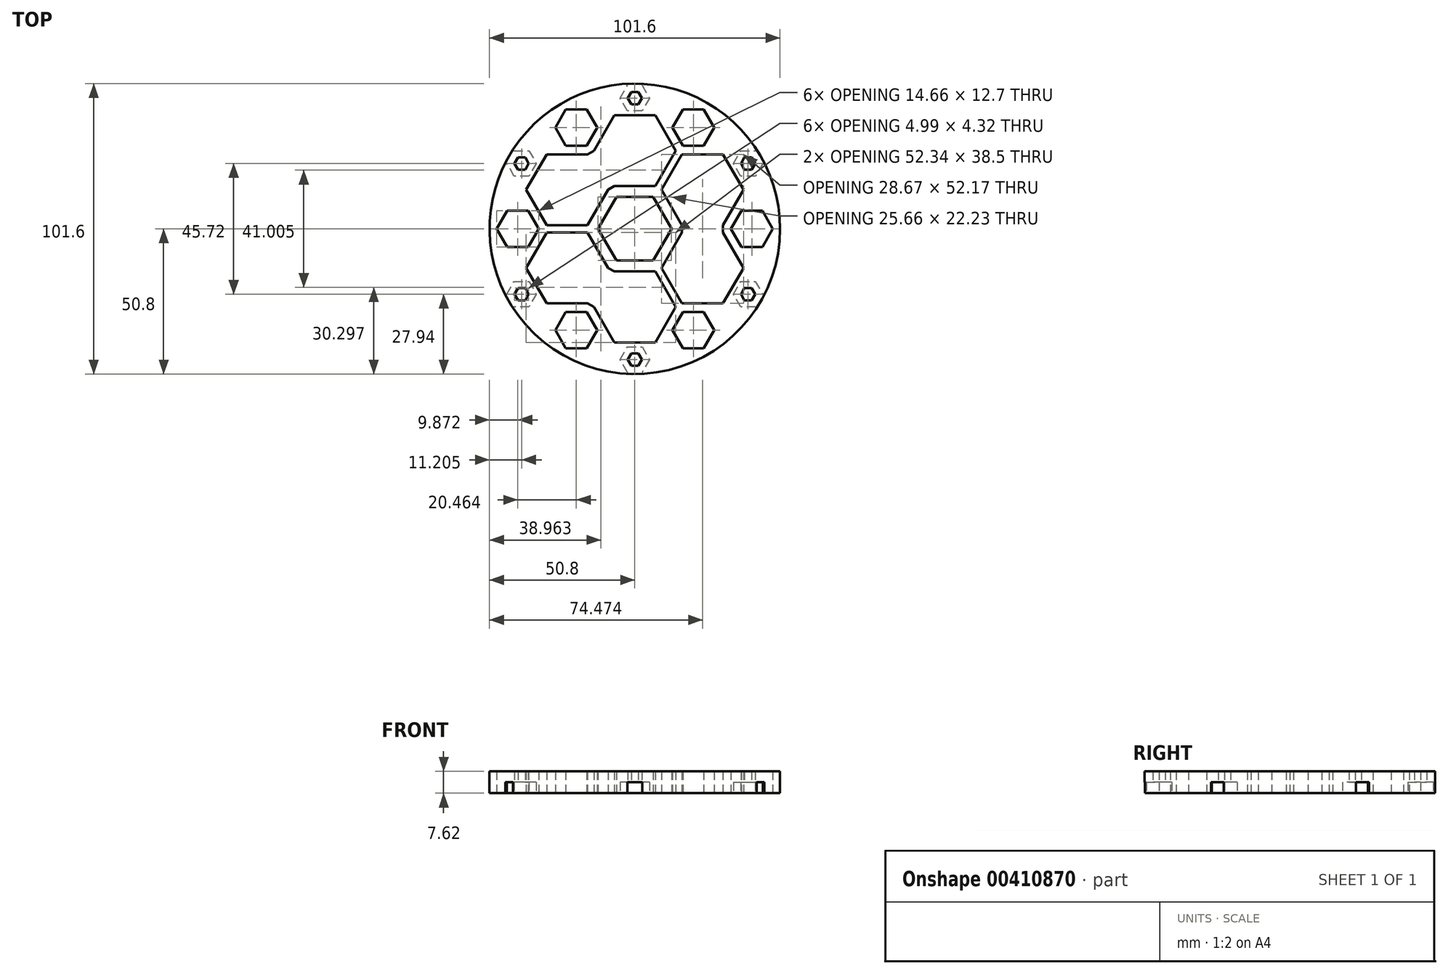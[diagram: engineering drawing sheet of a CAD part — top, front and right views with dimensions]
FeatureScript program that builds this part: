
annotation { "Feature Type Name" : "Feature", "Feature Type Description" : "" }
export const myFeature = defineFeature(function(context is Context, id is Id, definition is map)
    precondition{}
    {
        {
            var Q0;
            Q0=qCreatedBy(makeId("Top.planeOp"),FACE);
            var sketch = newSketch(context, id + "F0", { "sketchPlane" : qUnion([Q0])});
            skCircle(sketch, "E0", {"center": v(0, 0) * mm, "radius": 50.8 * mm});
            skCircle(sketch, "E1.cCircle", {"center": v(0, 0) * mm, "radius": 11.11 * mm, "construction": true});
            skLineSegment(sketch, "E1.0", {"start": v(-6.42, 11.11) * mm, "end": v(6.42, 11.11) * mm});
            skLineSegment(sketch, "E1.1", {"start": v(6.42, 11.11) * mm, "end": v(12.83, 0) * mm});
            skLineSegment(sketch, "E1.2", {"start": v(12.83, 0) * mm, "end": v(6.42, -11.11) * mm});
            skLineSegment(sketch, "E1.3", {"start": v(6.42, -11.11) * mm, "end": v(-6.42, -11.11) * mm});
            skLineSegment(sketch, "E1.4", {"start": v(-6.42, -11.11) * mm, "end": v(-12.83, 0) * mm});
            skLineSegment(sketch, "E1.5", {"start": v(-12.83, 0) * mm, "end": v(-6.42, 11.11) * mm});
            skPoint(sketch, "E1.0.midPoint", {"position": v(0, 11.11) * mm});
            skLineSegment(sketch, "E2", {"start": v(0, 0) * mm, "end": v(0, 45.72) * mm, "construction": true});
            skCircle(sketch, "E3.cCircle", {"center": v(0, 45.72) * mm, "radius": 2.16 * mm, "construction": true});
            skLineSegment(sketch, "E3.0", {"start": v(-1.25, 47.88) * mm, "end": v(1.25, 47.88) * mm});
            skLineSegment(sketch, "E3.1", {"start": v(1.25, 47.88) * mm, "end": v(2.5, 45.72) * mm});
            skLineSegment(sketch, "E3.2", {"start": v(2.5, 45.72) * mm, "end": v(1.25, 43.56) * mm});
            skLineSegment(sketch, "E3.3", {"start": v(1.25, 43.56) * mm, "end": v(-1.25, 43.56) * mm});
            skLineSegment(sketch, "E3.4", {"start": v(-1.25, 43.56) * mm, "end": v(-2.5, 45.72) * mm});
            skLineSegment(sketch, "E3.5", {"start": v(-2.5, 45.72) * mm, "end": v(-1.25, 47.88) * mm});
            skPoint(sketch, "E3.0.midPoint", {"position": v(0, 47.88) * mm});
            skLineSegment(sketch, "E4", {"start": v(0, 0) * mm, "end": v(39.6, -22.86) * mm, "construction": true});
            skCircle(sketch, "E5.cCircle", {"center": v(0, 27.34) * mm, "radius": 12.41 * mm, "construction": true});
            skLineSegment(sketch, "E5.0", {"start": v(-7.17, 39.75) * mm, "end": v(7.17, 39.75) * mm});
            skLineSegment(sketch, "E5.1", {"start": v(7.17, 39.75) * mm, "end": v(14.33, 27.34) * mm});
            skLineSegment(sketch, "E5.2", {"start": v(14.33, 27.34) * mm, "end": v(7.17, 14.92) * mm});
            skLineSegment(sketch, "E5.3", {"start": v(7.17, 14.92) * mm, "end": v(-7.17, 14.92) * mm});
            skLineSegment(sketch, "E5.4", {"start": v(-7.17, 14.92) * mm, "end": v(-14.33, 27.34) * mm});
            skLineSegment(sketch, "E5.5", {"start": v(-14.33, 27.34) * mm, "end": v(-7.17, 39.75) * mm});
            skPoint(sketch, "E5.0.midPoint", {"position": v(0, 39.75) * mm});
            skLineSegment(sketch, "E6.1.0", {"start": v(-38.35, 20.7) * mm, "end": v(-40.84, 20.7) * mm});
            skLineSegment(sketch, "E6.1.1", {"start": v(-37.1, 22.86) * mm, "end": v(-38.35, 20.7) * mm});
            skLineSegment(sketch, "E6.1.2", {"start": v(-38.35, 25.02) * mm, "end": v(-37.1, 22.86) * mm});
            skLineSegment(sketch, "E6.1.3", {"start": v(-40.84, 25.02) * mm, "end": v(-38.35, 25.02) * mm});
            skLineSegment(sketch, "E6.1.4", {"start": v(-42.09, 22.86) * mm, "end": v(-40.84, 25.02) * mm});
            skLineSegment(sketch, "E6.1.5", {"start": v(-40.84, 20.7) * mm, "end": v(-42.09, 22.86) * mm});
            skLineSegment(sketch, "E6.1.6", {"start": v(-16.5, 26.08) * mm, "end": v(-9.34, 13.67) * mm});
            skLineSegment(sketch, "E6.1.7", {"start": v(-30.84, 26.08) * mm, "end": v(-16.5, 26.08) * mm});
            skLineSegment(sketch, "E6.1.8", {"start": v(-38, 13.67) * mm, "end": v(-30.84, 26.08) * mm});
            skLineSegment(sketch, "E6.1.9", {"start": v(-30.84, 1.25) * mm, "end": v(-38, 13.67) * mm});
            skLineSegment(sketch, "E6.1.10", {"start": v(-16.5, 1.25) * mm, "end": v(-30.84, 1.25) * mm});
            skLineSegment(sketch, "E6.1.11", {"start": v(-9.34, 13.67) * mm, "end": v(-16.5, 1.25) * mm});
            skLineSegment(sketch, "E6.2.0", {"start": v(-37.1, -22.86) * mm, "end": v(-38.35, -25.02) * mm});
            skLineSegment(sketch, "E6.2.1", {"start": v(-38.35, -20.7) * mm, "end": v(-37.1, -22.86) * mm});
            skLineSegment(sketch, "E6.2.2", {"start": v(-40.84, -20.7) * mm, "end": v(-38.35, -20.7) * mm});
            skLineSegment(sketch, "E6.2.3", {"start": v(-42.09, -22.86) * mm, "end": v(-40.84, -20.7) * mm});
            skLineSegment(sketch, "E6.2.4", {"start": v(-40.84, -25.02) * mm, "end": v(-42.09, -22.86) * mm});
            skLineSegment(sketch, "E6.2.5", {"start": v(-38.35, -25.02) * mm, "end": v(-40.84, -25.02) * mm});
            skLineSegment(sketch, "E6.2.6", {"start": v(-30.84, -1.25) * mm, "end": v(-16.5, -1.25) * mm});
            skLineSegment(sketch, "E6.2.7", {"start": v(-38, -13.67) * mm, "end": v(-30.84, -1.25) * mm});
            skLineSegment(sketch, "E6.2.8", {"start": v(-30.84, -26.08) * mm, "end": v(-38, -13.67) * mm});
            skLineSegment(sketch, "E6.2.9", {"start": v(-16.5, -26.08) * mm, "end": v(-30.84, -26.08) * mm});
            skLineSegment(sketch, "E6.2.10", {"start": v(-9.34, -13.67) * mm, "end": v(-16.5, -26.08) * mm});
            skLineSegment(sketch, "E6.2.11", {"start": v(-16.5, -1.25) * mm, "end": v(-9.34, -13.67) * mm});
            skLineSegment(sketch, "E7.1.3.0", {"start": v(1.25, -43.56) * mm, "end": v(2.5, -45.72) * mm});
            skLineSegment(sketch, "E7.3.3.0", {"start": v(-1.25, -43.56) * mm, "end": v(1.25, -43.56) * mm});
            skLineSegment(sketch, "E7.6.3.0", {"start": v(-2.5, -45.72) * mm, "end": v(-1.25, -43.56) * mm});
            skLineSegment(sketch, "E7.9.3.0", {"start": v(-1.25, -47.88) * mm, "end": v(-2.5, -45.72) * mm});
            skLineSegment(sketch, "E7.12.3.0", {"start": v(1.25, -47.88) * mm, "end": v(-1.25, -47.88) * mm});
            skLineSegment(sketch, "E7.15.3.0", {"start": v(2.5, -45.72) * mm, "end": v(1.25, -47.88) * mm});
            skLineSegment(sketch, "E7.18.3.0", {"start": v(-14.33, -27.34) * mm, "end": v(-7.17, -14.92) * mm});
            skLineSegment(sketch, "E7.21.3.0", {"start": v(-7.17, -39.75) * mm, "end": v(-14.33, -27.34) * mm});
            skLineSegment(sketch, "E7.24.3.0", {"start": v(7.17, -39.75) * mm, "end": v(-7.17, -39.75) * mm});
            skLineSegment(sketch, "E7.27.3.0", {"start": v(14.33, -27.34) * mm, "end": v(7.17, -39.75) * mm});
            skLineSegment(sketch, "E7.30.3.0", {"start": v(7.17, -14.92) * mm, "end": v(14.33, -27.34) * mm});
            skLineSegment(sketch, "E7.33.3.0", {"start": v(-7.17, -14.92) * mm, "end": v(7.17, -14.92) * mm});
            skLineSegment(sketch, "E7.1.4.0", {"start": v(38.35, -20.7) * mm, "end": v(40.84, -20.7) * mm});
            skLineSegment(sketch, "E7.3.4.0", {"start": v(37.1, -22.86) * mm, "end": v(38.35, -20.7) * mm});
            skLineSegment(sketch, "E7.6.4.0", {"start": v(38.35, -25.02) * mm, "end": v(37.1, -22.86) * mm});
            skLineSegment(sketch, "E7.9.4.0", {"start": v(40.84, -25.02) * mm, "end": v(38.35, -25.02) * mm});
            skLineSegment(sketch, "E7.12.4.0", {"start": v(42.09, -22.86) * mm, "end": v(40.84, -25.02) * mm});
            skLineSegment(sketch, "E7.15.4.0", {"start": v(40.84, -20.7) * mm, "end": v(42.09, -22.86) * mm});
            skLineSegment(sketch, "E7.18.4.0", {"start": v(16.5, -26.08) * mm, "end": v(9.34, -13.67) * mm});
            skLineSegment(sketch, "E7.21.4.0", {"start": v(30.84, -26.08) * mm, "end": v(16.5, -26.08) * mm});
            skLineSegment(sketch, "E7.24.4.0", {"start": v(38, -13.67) * mm, "end": v(30.84, -26.08) * mm});
            skLineSegment(sketch, "E7.27.4.0", {"start": v(30.84, -1.25) * mm, "end": v(38, -13.67) * mm});
            skLineSegment(sketch, "E7.30.4.0", {"start": v(16.5, -1.25) * mm, "end": v(30.84, -1.25) * mm});
            skLineSegment(sketch, "E7.33.4.0", {"start": v(9.34, -13.67) * mm, "end": v(16.5, -1.25) * mm});
            skLineSegment(sketch, "E7.1.5.0", {"start": v(37.1, 22.86) * mm, "end": v(38.35, 25.02) * mm});
            skLineSegment(sketch, "E7.3.5.0", {"start": v(38.35, 20.7) * mm, "end": v(37.1, 22.86) * mm});
            skLineSegment(sketch, "E7.6.5.0", {"start": v(40.84, 20.7) * mm, "end": v(38.35, 20.7) * mm});
            skLineSegment(sketch, "E7.9.5.0", {"start": v(42.09, 22.86) * mm, "end": v(40.84, 20.7) * mm});
            skLineSegment(sketch, "E7.12.5.0", {"start": v(40.84, 25.02) * mm, "end": v(42.09, 22.86) * mm});
            skLineSegment(sketch, "E7.15.5.0", {"start": v(38.35, 25.02) * mm, "end": v(40.84, 25.02) * mm});
            skLineSegment(sketch, "E7.18.5.0", {"start": v(30.84, 1.25) * mm, "end": v(16.5, 1.25) * mm});
            skLineSegment(sketch, "E7.21.5.0", {"start": v(38, 13.67) * mm, "end": v(30.84, 1.25) * mm});
            skLineSegment(sketch, "E7.24.5.0", {"start": v(30.84, 26.08) * mm, "end": v(38, 13.67) * mm});
            skLineSegment(sketch, "E7.27.5.0", {"start": v(16.5, 26.08) * mm, "end": v(30.84, 26.08) * mm});
            skLineSegment(sketch, "E7.30.5.0", {"start": v(9.34, 13.67) * mm, "end": v(16.5, 26.08) * mm});
            skLineSegment(sketch, "E7.33.5.0", {"start": v(16.5, 1.25) * mm, "end": v(9.34, 13.67) * mm});
            skLineSegment(sketch, "E8", {"start": v(-6.42, 11.11) * mm, "end": v(-25.4, 44) * mm, "construction": true});
            skCircle(sketch, "E9.cCircle", {"center": v(-20.46, 35.44) * mm, "radius": 6.35 * mm, "construction": true});
            skLineSegment(sketch, "E9.0", {"start": v(-16.8, 41.8) * mm, "end": v(-13.13, 35.44) * mm});
            skLineSegment(sketch, "E9.1", {"start": v(-13.13, 35.44) * mm, "end": v(-16.8, 29.1) * mm});
            skLineSegment(sketch, "E9.2", {"start": v(-16.8, 29.1) * mm, "end": v(-24.13, 29.1) * mm});
            skLineSegment(sketch, "E9.3", {"start": v(-24.13, 29.1) * mm, "end": v(-27.8, 35.44) * mm});
            skLineSegment(sketch, "E9.4", {"start": v(-27.8, 35.44) * mm, "end": v(-24.13, 41.8) * mm});
            skLineSegment(sketch, "E9.5", {"start": v(-24.13, 41.8) * mm, "end": v(-16.8, 41.8) * mm});
            skPoint(sketch, "E9.0.midPoint", {"position": v(-14.96, 38.62) * mm});
            skLineSegment(sketch, "E10.1.0", {"start": v(-48.26, 0) * mm, "end": v(-44.6, 6.35) * mm});
            skLineSegment(sketch, "E10.1.1", {"start": v(-44.6, 6.35) * mm, "end": v(-37.26, 6.35) * mm});
            skLineSegment(sketch, "E10.1.2", {"start": v(-37.26, 6.35) * mm, "end": v(-33.6, 0) * mm});
            skLineSegment(sketch, "E10.1.3", {"start": v(-33.6, 0) * mm, "end": v(-37.26, -6.35) * mm});
            skLineSegment(sketch, "E10.1.4", {"start": v(-37.26, -6.35) * mm, "end": v(-44.6, -6.35) * mm});
            skLineSegment(sketch, "E10.1.5", {"start": v(-44.6, -6.35) * mm, "end": v(-48.26, 0) * mm});
            skLineSegment(sketch, "E10.2.0", {"start": v(-24.13, -41.8) * mm, "end": v(-27.8, -35.44) * mm});
            skLineSegment(sketch, "E10.2.1", {"start": v(-27.8, -35.44) * mm, "end": v(-24.13, -29.1) * mm});
            skLineSegment(sketch, "E10.2.2", {"start": v(-24.13, -29.1) * mm, "end": v(-16.8, -29.1) * mm});
            skLineSegment(sketch, "E10.2.3", {"start": v(-16.8, -29.1) * mm, "end": v(-13.13, -35.44) * mm});
            skLineSegment(sketch, "E10.2.4", {"start": v(-13.13, -35.44) * mm, "end": v(-16.8, -41.8) * mm});
            skLineSegment(sketch, "E10.2.5", {"start": v(-16.8, -41.8) * mm, "end": v(-24.13, -41.8) * mm});
            skLineSegment(sketch, "E10.3.0", {"start": v(24.13, -41.8) * mm, "end": v(16.8, -41.8) * mm});
            skLineSegment(sketch, "E10.3.1", {"start": v(16.8, -41.8) * mm, "end": v(13.13, -35.44) * mm});
            skLineSegment(sketch, "E10.3.2", {"start": v(13.13, -35.44) * mm, "end": v(16.8, -29.1) * mm});
            skLineSegment(sketch, "E10.3.3", {"start": v(16.8, -29.1) * mm, "end": v(24.13, -29.1) * mm});
            skLineSegment(sketch, "E10.3.4", {"start": v(24.13, -29.1) * mm, "end": v(27.8, -35.44) * mm});
            skLineSegment(sketch, "E10.3.5", {"start": v(27.8, -35.44) * mm, "end": v(24.13, -41.8) * mm});
            skLineSegment(sketch, "E10.4.0", {"start": v(48.26, 0) * mm, "end": v(44.6, -6.35) * mm});
            skLineSegment(sketch, "E10.4.1", {"start": v(44.6, -6.35) * mm, "end": v(37.26, -6.35) * mm});
            skLineSegment(sketch, "E10.4.2", {"start": v(37.26, -6.35) * mm, "end": v(33.6, 0) * mm});
            skLineSegment(sketch, "E10.4.3", {"start": v(33.6, 0) * mm, "end": v(37.26, 6.35) * mm});
            skLineSegment(sketch, "E10.4.4", {"start": v(37.26, 6.35) * mm, "end": v(44.6, 6.35) * mm});
            skLineSegment(sketch, "E10.4.5", {"start": v(44.6, 6.35) * mm, "end": v(48.26, 0) * mm});
            skLineSegment(sketch, "E10.5.0", {"start": v(24.13, 41.8) * mm, "end": v(27.8, 35.44) * mm});
            skLineSegment(sketch, "E10.5.1", {"start": v(27.8, 35.44) * mm, "end": v(24.13, 29.1) * mm});
            skLineSegment(sketch, "E10.5.2", {"start": v(24.13, 29.1) * mm, "end": v(16.8, 29.1) * mm});
            skLineSegment(sketch, "E10.5.3", {"start": v(16.8, 29.1) * mm, "end": v(13.13, 35.44) * mm});
            skLineSegment(sketch, "E10.5.4", {"start": v(13.13, 35.44) * mm, "end": v(16.8, 41.8) * mm});
            skLineSegment(sketch, "E10.5.5", {"start": v(16.8, 41.8) * mm, "end": v(24.13, 41.8) * mm});
            skCircle(sketch, "E11.cCircle", {"center": v(0, 45.72) * mm, "radius": 4.45 * mm, "construction": true});
            skLineSegment(sketch, "E11.0", {"start": v(-2.57, 50.16) * mm, "end": v(2.57, 50.16) * mm});
            skLineSegment(sketch, "E11.1", {"start": v(2.57, 50.16) * mm, "end": v(5.13, 45.72) * mm});
            skLineSegment(sketch, "E11.2", {"start": v(5.13, 45.72) * mm, "end": v(2.57, 41.28) * mm});
            skLineSegment(sketch, "E11.3", {"start": v(2.57, 41.28) * mm, "end": v(-2.57, 41.28) * mm});
            skLineSegment(sketch, "E11.4", {"start": v(-2.57, 41.28) * mm, "end": v(-5.13, 45.72) * mm});
            skLineSegment(sketch, "E11.5", {"start": v(-5.13, 45.72) * mm, "end": v(-2.57, 50.16) * mm});
            skPoint(sketch, "E11.0.midPoint", {"position": v(0, 50.16) * mm});
            skLineSegment(sketch, "E12.1.0", {"start": v(-44.73, 22.86) * mm, "end": v(-42.16, 27.3) * mm});
            skLineSegment(sketch, "E12.1.1", {"start": v(-42.16, 18.42) * mm, "end": v(-44.73, 22.86) * mm});
            skLineSegment(sketch, "E12.1.2", {"start": v(-37.03, 18.42) * mm, "end": v(-42.16, 18.42) * mm});
            skLineSegment(sketch, "E12.1.3", {"start": v(-34.46, 22.86) * mm, "end": v(-37.03, 18.42) * mm});
            skLineSegment(sketch, "E12.1.4", {"start": v(-37.03, 27.3) * mm, "end": v(-34.46, 22.86) * mm});
            skLineSegment(sketch, "E12.1.5", {"start": v(-42.16, 27.3) * mm, "end": v(-37.03, 27.3) * mm});
            skLineSegment(sketch, "E12.2.0", {"start": v(-42.16, -27.3) * mm, "end": v(-44.73, -22.86) * mm});
            skLineSegment(sketch, "E12.2.1", {"start": v(-37.03, -27.3) * mm, "end": v(-42.16, -27.3) * mm});
            skLineSegment(sketch, "E12.2.2", {"start": v(-34.46, -22.86) * mm, "end": v(-37.03, -27.3) * mm});
            skLineSegment(sketch, "E12.2.3", {"start": v(-37.03, -18.41) * mm, "end": v(-34.46, -22.86) * mm});
            skLineSegment(sketch, "E12.2.4", {"start": v(-42.16, -18.41) * mm, "end": v(-37.03, -18.41) * mm});
            skLineSegment(sketch, "E12.2.5", {"start": v(-44.73, -22.86) * mm, "end": v(-42.16, -18.41) * mm});
            skLineSegment(sketch, "E13.1.3.0", {"start": v(2.57, -50.16) * mm, "end": v(-2.57, -50.16) * mm});
            skLineSegment(sketch, "E13.3.3.0", {"start": v(5.13, -45.72) * mm, "end": v(2.57, -50.16) * mm});
            skLineSegment(sketch, "E13.6.3.0", {"start": v(2.57, -41.28) * mm, "end": v(5.13, -45.72) * mm});
            skLineSegment(sketch, "E13.9.3.0", {"start": v(-2.57, -41.28) * mm, "end": v(2.57, -41.28) * mm});
            skLineSegment(sketch, "E13.12.3.0", {"start": v(-5.13, -45.72) * mm, "end": v(-2.57, -41.28) * mm});
            skLineSegment(sketch, "E13.15.3.0", {"start": v(-2.57, -50.16) * mm, "end": v(-5.13, -45.72) * mm});
            skLineSegment(sketch, "E13.1.4.0", {"start": v(44.73, -22.86) * mm, "end": v(42.16, -27.3) * mm});
            skLineSegment(sketch, "E13.3.4.0", {"start": v(42.16, -18.42) * mm, "end": v(44.73, -22.86) * mm});
            skLineSegment(sketch, "E13.6.4.0", {"start": v(37.03, -18.42) * mm, "end": v(42.16, -18.42) * mm});
            skLineSegment(sketch, "E13.9.4.0", {"start": v(34.46, -22.86) * mm, "end": v(37.03, -18.42) * mm});
            skLineSegment(sketch, "E13.12.4.0", {"start": v(37.03, -27.3) * mm, "end": v(34.46, -22.86) * mm});
            skLineSegment(sketch, "E13.15.4.0", {"start": v(42.16, -27.3) * mm, "end": v(37.03, -27.3) * mm});
            skLineSegment(sketch, "E13.1.5.0", {"start": v(42.16, 27.3) * mm, "end": v(44.73, 22.86) * mm});
            skLineSegment(sketch, "E13.3.5.0", {"start": v(37.03, 27.3) * mm, "end": v(42.16, 27.3) * mm});
            skLineSegment(sketch, "E13.6.5.0", {"start": v(34.46, 22.86) * mm, "end": v(37.03, 27.3) * mm});
            skLineSegment(sketch, "E13.9.5.0", {"start": v(37.03, 18.42) * mm, "end": v(34.46, 22.86) * mm});
            skLineSegment(sketch, "E13.12.5.0", {"start": v(42.16, 18.42) * mm, "end": v(37.03, 18.42) * mm});
            skLineSegment(sketch, "E13.15.5.0", {"start": v(44.73, 22.86) * mm, "end": v(42.16, 18.42) * mm});
            skLineSegment(sketch, "E14", {"start": v(-44.73, 22.86) * mm, "end": v(-45.22, 23.15) * mm});
            skLineSegment(sketch, "E15", {"start": v(-42.16, 27.3) * mm, "end": v(-42.65, 27.6) * mm});
            skLineSegment(sketch, "E16.1.0", {"start": v(-42.16, -27.3) * mm, "end": v(-42.65, -27.6) * mm});
            skLineSegment(sketch, "E16.1.1", {"start": v(-44.73, -22.86) * mm, "end": v(-45.22, -23.15) * mm});
            skLineSegment(sketch, "E16.2.0", {"start": v(2.57, -50.16) * mm, "end": v(2.57, -50.74) * mm});
            skLineSegment(sketch, "E16.2.1", {"start": v(-2.57, -50.16) * mm, "end": v(-2.57, -50.74) * mm});
            skLineSegment(sketch, "E16.3.0", {"start": v(44.73, -22.86) * mm, "end": v(45.22, -23.15) * mm});
            skLineSegment(sketch, "E16.3.1", {"start": v(42.16, -27.3) * mm, "end": v(42.65, -27.6) * mm});
            skLineSegment(sketch, "E16.4.0", {"start": v(42.16, 27.3) * mm, "end": v(42.65, 27.6) * mm});
            skLineSegment(sketch, "E16.4.1", {"start": v(44.73, 22.86) * mm, "end": v(45.22, 23.15) * mm});
            skLineSegment(sketch, "E16.5.0", {"start": v(-2.57, 50.16) * mm, "end": v(-2.57, 50.74) * mm});
            skLineSegment(sketch, "E16.5.1", {"start": v(2.57, 50.16) * mm, "end": v(2.57, 50.74) * mm});
            skSolve(sketch);
        }
        {
            var Q0;
            Q0=makeQuery(id+"F0.imprint","IMPRINT",FACE,{"disambiguationData":[TD([[makeQuery(id+"F0.imprint","IMPRINT",EDGE,{"derivedFrom":sQuery(id+"F0.wireOp",EDGE,"E0")}),1.0]])]});
            var Q1;
            Q1=makeQuery(id+"F0.imprint","IMPRINT",FACE,{"disambiguationData":[TD([[makeQuery(id+"F0.imprint","IMPRINT",EDGE,{"derivedFrom":sQuery(id+"F0.wireOp",EDGE,"E3.0")}),1.0]])]});
            var Q2;
            Q2=makeQuery(id+"F0.imprint","IMPRINT",FACE,{"disambiguationData":[TD([[makeQuery(id+"F0.imprint","IMPRINT",EDGE,{"derivedFrom":sQuery(id+"F0.wireOp",EDGE,"E7.1.5.0")}),1.0]])]});
            var Q3;
            Q3=makeQuery(id+"F0.imprint","IMPRINT",FACE,{"disambiguationData":[TD([[makeQuery(id+"F0.imprint","IMPRINT",EDGE,{"derivedFrom":sQuery(id+"F0.wireOp",EDGE,"E7.1.4.0")}),1.0]])]});
            var Q4;
            Q4=makeQuery(id+"F0.imprint","IMPRINT",FACE,{"disambiguationData":[TD([[makeQuery(id+"F0.imprint","IMPRINT",EDGE,{"derivedFrom":sQuery(id+"F0.wireOp",EDGE,"E7.1.3.0")}),1.0]])]});
            var Q5;
            Q5=makeQuery(id+"F0.imprint","IMPRINT",FACE,{"disambiguationData":[TD([[makeQuery(id+"F0.imprint","IMPRINT",EDGE,{"derivedFrom":sQuery(id+"F0.wireOp",EDGE,"E6.2.0")}),1.0]])]});
            var Q6;
            Q6=makeQuery(id+"F0.imprint","IMPRINT",FACE,{"disambiguationData":[TD([[makeQuery(id+"F0.imprint","IMPRINT",EDGE,{"derivedFrom":sQuery(id+"F0.wireOp",EDGE,"E6.1.0")}),1.0]])]});
            var Q7;
            Q7=makeQuery(id+"F0.imprint","IMPRINT",FACE,{"disambiguationData":[TD([[makeQuery(id+"F0.imprint","IMPRINT",EDGE,{"derivedFrom":sQuery(id+"F0.wireOp",EDGE,"E12.1.0")}),1.0]])]});
            var Q8;
            Q8=makeQuery(id+"F0.imprint","IMPRINT",FACE,{"disambiguationData":[TD([[makeQuery(id+"F0.imprint","IMPRINT",EDGE,{"derivedFrom":sQuery(id+"F0.wireOp",EDGE,"E12.2.0")}),1.0]])]});
            var Q9;
            Q9=makeQuery(id+"F0.imprint","IMPRINT",FACE,{"disambiguationData":[TD([[makeQuery(id+"F0.imprint","IMPRINT",EDGE,{"derivedFrom":sQuery(id+"F0.wireOp",EDGE,"E13.1.3.0")}),1.0]])]});
            var Q10;
            Q10=makeQuery(id+"F0.imprint","IMPRINT",FACE,{"disambiguationData":[TD([[makeQuery(id+"F0.imprint","IMPRINT",EDGE,{"derivedFrom":sQuery(id+"F0.wireOp",EDGE,"E13.1.4.0")}),1.0]])]});
            var Q11;
            Q11=makeQuery(id+"F0.imprint","IMPRINT",FACE,{"disambiguationData":[TD([[makeQuery(id+"F0.imprint","IMPRINT",EDGE,{"derivedFrom":sQuery(id+"F0.wireOp",EDGE,"E13.1.5.0")}),1.0]])]});
            var Q12;
            Q12=makeQuery(id+"F0.imprint","IMPRINT",FACE,{"disambiguationData":[TD([[makeQuery(id+"F0.imprint","IMPRINT",EDGE,{"derivedFrom":sQuery(id+"F0.wireOp",EDGE,"E11.0")}),1.0]])]});
            extrude(context, id + "F1", {"entities" : qUnion([Q0, Q1, Q2, Q3, Q4, Q5, Q6, Q7, Q8, Q9, Q10, Q11, Q12]), "depth" : 7.62 * mm});
        }
        {
            var Q0;
            Q0=makeQuery(id+"F0.imprint","IMPRINT",FACE,{"disambiguationData":[TD([[makeQuery(id+"F0.imprint","IMPRINT",EDGE,{"derivedFrom":sQuery(id+"F0.wireOp",EDGE,"E3.0")}),1.0]])]});
            var Q1;
            Q1=makeQuery(id+"F0.imprint","IMPRINT",FACE,{"disambiguationData":[TD([[makeQuery(id+"F0.imprint","IMPRINT",EDGE,{"derivedFrom":sQuery(id+"F0.wireOp",EDGE,"E7.1.5.0")}),1.0]])]});
            var Q2;
            Q2=makeQuery(id+"F0.imprint","IMPRINT",FACE,{"disambiguationData":[TD([[makeQuery(id+"F0.imprint","IMPRINT",EDGE,{"derivedFrom":sQuery(id+"F0.wireOp",EDGE,"E7.1.4.0")}),1.0]])]});
            var Q3;
            Q3=makeQuery(id+"F0.imprint","IMPRINT",FACE,{"disambiguationData":[TD([[makeQuery(id+"F0.imprint","IMPRINT",EDGE,{"derivedFrom":sQuery(id+"F0.wireOp",EDGE,"E7.1.3.0")}),1.0]])]});
            var Q4;
            Q4=makeQuery(id+"F0.imprint","IMPRINT",FACE,{"disambiguationData":[TD([[makeQuery(id+"F0.imprint","IMPRINT",EDGE,{"derivedFrom":sQuery(id+"F0.wireOp",EDGE,"E6.2.0")}),1.0]])]});
            var Q5;
            Q5=makeQuery(id+"F0.imprint","IMPRINT",FACE,{"disambiguationData":[TD([[makeQuery(id+"F0.imprint","IMPRINT",EDGE,{"derivedFrom":sQuery(id+"F0.wireOp",EDGE,"E6.1.0")}),1.0]])]});
            var Q6;
            Q6=makeQuery(id+"F0.imprint","IMPRINT",FACE,{"disambiguationData":[TD([[makeQuery(id+"F0.imprint","IMPRINT",EDGE,{"derivedFrom":sQuery(id+"F0.wireOp",EDGE,"E13.1.4.0")}),1.0]])]});
            var Q7;
            Q7=makeQuery(id+"F0.imprint","IMPRINT",FACE,{"disambiguationData":[TD([[makeQuery(id+"F0.imprint","IMPRINT",EDGE,{"derivedFrom":sQuery(id+"F0.wireOp",EDGE,"E13.1.3.0")}),1.0]])]});
            var Q8;
            Q8=makeQuery(id+"F0.imprint","IMPRINT",FACE,{"disambiguationData":[TD([[makeQuery(id+"F0.imprint","IMPRINT",EDGE,{"derivedFrom":sQuery(id+"F0.wireOp",EDGE,"E12.2.0")}),1.0]])]});
            var Q9;
            Q9=makeQuery(id+"F0.imprint","IMPRINT",FACE,{"disambiguationData":[TD([[makeQuery(id+"F0.imprint","IMPRINT",EDGE,{"derivedFrom":sQuery(id+"F0.wireOp",EDGE,"E12.1.0")}),1.0]])]});
            var Q10;
            Q10=makeQuery(id+"F0.imprint","IMPRINT",FACE,{"disambiguationData":[TD([[makeQuery(id+"F0.imprint","IMPRINT",EDGE,{"derivedFrom":sQuery(id+"F0.wireOp",EDGE,"E11.0")}),1.0]])]});
            var Q11;
            Q11=makeQuery(id+"F0.imprint","IMPRINT",FACE,{"disambiguationData":[TD([[makeQuery(id+"F0.imprint","IMPRINT",EDGE,{"derivedFrom":sQuery(id+"F0.wireOp",EDGE,"E13.1.5.0")}),1.0]])]});
            extrude(context, id + "F2", {"entities" : qUnion([Q0, Q1, Q2, Q3, Q4, Q5, Q6, Q7, Q8, Q9, Q10, Q11]), "operationType" : NewBodyOperationType.REMOVE, "depth" : 3.8 * mm});
        }
        {
            var Q0;
            Q0=makeQuery(id+"F1.opExtrude","CAP_FACE",FACE,{"disambiguationData":[OSD([sQuery(id+"F0.wireOp",EDGE,"E0"),sQuery(id+"F0.wireOp",EDGE,"E1.0"),sQuery(id+"F0.wireOp",EDGE,"E1.1"),sQuery(id+"F0.wireOp",EDGE,"E1.2"),sQuery(id+"F0.wireOp",EDGE,"E1.3"),sQuery(id+"F0.wireOp",EDGE,"E1.4"),sQuery(id+"F0.wireOp",EDGE,"E1.5"),sQuery(id+"F0.wireOp",EDGE,"E3.0"),sQuery(id+"F0.wireOp",EDGE,"E3.1"),sQuery(id+"F0.wireOp",EDGE,"E3.2"),sQuery(id+"F0.wireOp",EDGE,"E3.3"),sQuery(id+"F0.wireOp",EDGE,"E3.4"),sQuery(id+"F0.wireOp",EDGE,"E3.5"),sQuery(id+"F0.wireOp",EDGE,"E5.0"),sQuery(id+"F0.wireOp",EDGE,"E5.1"),sQuery(id+"F0.wireOp",EDGE,"E5.2"),sQuery(id+"F0.wireOp",EDGE,"E5.3"),sQuery(id+"F0.wireOp",EDGE,"E5.4"),sQuery(id+"F0.wireOp",EDGE,"E5.5"),sQuery(id+"F0.wireOp",EDGE,"E6.1.0"),sQuery(id+"F0.wireOp",EDGE,"E6.1.1"),sQuery(id+"F0.wireOp",EDGE,"E6.1.2"),sQuery(id+"F0.wireOp",EDGE,"E6.1.3"),sQuery(id+"F0.wireOp",EDGE,"E6.1.4"),sQuery(id+"F0.wireOp",EDGE,"E6.1.5"),sQuery(id+"F0.wireOp",EDGE,"E6.1.6"),sQuery(id+"F0.wireOp",EDGE,"E6.1.7"),sQuery(id+"F0.wireOp",EDGE,"E6.1.8"),sQuery(id+"F0.wireOp",EDGE,"E6.1.9"),sQuery(id+"F0.wireOp",EDGE,"E6.1.10"),sQuery(id+"F0.wireOp",EDGE,"E6.1.11"),sQuery(id+"F0.wireOp",EDGE,"E6.2.0"),sQuery(id+"F0.wireOp",EDGE,"E6.2.1"),sQuery(id+"F0.wireOp",EDGE,"E6.2.2"),sQuery(id+"F0.wireOp",EDGE,"E6.2.3"),sQuery(id+"F0.wireOp",EDGE,"E6.2.4"),sQuery(id+"F0.wireOp",EDGE,"E6.2.5"),sQuery(id+"F0.wireOp",EDGE,"E6.2.6"),sQuery(id+"F0.wireOp",EDGE,"E6.2.7"),sQuery(id+"F0.wireOp",EDGE,"E6.2.8"),sQuery(id+"F0.wireOp",EDGE,"E6.2.9"),sQuery(id+"F0.wireOp",EDGE,"E6.2.10"),sQuery(id+"F0.wireOp",EDGE,"E6.2.11"),sQuery(id+"F0.wireOp",EDGE,"E7.1.3.0"),sQuery(id+"F0.wireOp",EDGE,"E7.3.3.0"),sQuery(id+"F0.wireOp",EDGE,"E7.6.3.0"),sQuery(id+"F0.wireOp",EDGE,"E7.9.3.0"),sQuery(id+"F0.wireOp",EDGE,"E7.12.3.0"),sQuery(id+"F0.wireOp",EDGE,"E7.15.3.0"),sQuery(id+"F0.wireOp",EDGE,"E7.18.3.0"),sQuery(id+"F0.wireOp",EDGE,"E7.21.3.0"),sQuery(id+"F0.wireOp",EDGE,"E7.24.3.0"),sQuery(id+"F0.wireOp",EDGE,"E7.27.3.0"),sQuery(id+"F0.wireOp",EDGE,"E7.30.3.0"),sQuery(id+"F0.wireOp",EDGE,"E7.33.3.0"),sQuery(id+"F0.wireOp",EDGE,"E7.1.4.0"),sQuery(id+"F0.wireOp",EDGE,"E7.3.4.0"),sQuery(id+"F0.wireOp",EDGE,"E7.6.4.0"),sQuery(id+"F0.wireOp",EDGE,"E7.9.4.0"),sQuery(id+"F0.wireOp",EDGE,"E7.12.4.0"),sQuery(id+"F0.wireOp",EDGE,"E7.15.4.0"),sQuery(id+"F0.wireOp",EDGE,"E7.18.4.0"),sQuery(id+"F0.wireOp",EDGE,"E7.21.4.0"),sQuery(id+"F0.wireOp",EDGE,"E7.24.4.0"),sQuery(id+"F0.wireOp",EDGE,"E7.27.4.0"),sQuery(id+"F0.wireOp",EDGE,"E7.30.4.0"),sQuery(id+"F0.wireOp",EDGE,"E7.33.4.0"),sQuery(id+"F0.wireOp",EDGE,"E7.1.5.0"),sQuery(id+"F0.wireOp",EDGE,"E7.3.5.0"),sQuery(id+"F0.wireOp",EDGE,"E7.6.5.0"),sQuery(id+"F0.wireOp",EDGE,"E7.9.5.0"),sQuery(id+"F0.wireOp",EDGE,"E7.12.5.0"),sQuery(id+"F0.wireOp",EDGE,"E7.15.5.0"),sQuery(id+"F0.wireOp",EDGE,"E7.18.5.0"),sQuery(id+"F0.wireOp",EDGE,"E7.21.5.0"),sQuery(id+"F0.wireOp",EDGE,"E7.24.5.0"),sQuery(id+"F0.wireOp",EDGE,"E7.27.5.0"),sQuery(id+"F0.wireOp",EDGE,"E7.30.5.0"),sQuery(id+"F0.wireOp",EDGE,"E7.33.5.0"),sQuery(id+"F0.wireOp",EDGE,"E9.0"),sQuery(id+"F0.wireOp",EDGE,"E9.1"),sQuery(id+"F0.wireOp",EDGE,"E9.2"),sQuery(id+"F0.wireOp",EDGE,"E9.3"),sQuery(id+"F0.wireOp",EDGE,"E9.4"),sQuery(id+"F0.wireOp",EDGE,"E9.5"),sQuery(id+"F0.wireOp",EDGE,"E10.1.0"),sQuery(id+"F0.wireOp",EDGE,"E10.1.1"),sQuery(id+"F0.wireOp",EDGE,"E10.1.2"),sQuery(id+"F0.wireOp",EDGE,"E10.1.3"),sQuery(id+"F0.wireOp",EDGE,"E10.1.4"),sQuery(id+"F0.wireOp",EDGE,"E10.1.5"),sQuery(id+"F0.wireOp",EDGE,"E10.2.0"),sQuery(id+"F0.wireOp",EDGE,"E10.2.1"),sQuery(id+"F0.wireOp",EDGE,"E10.2.2"),sQuery(id+"F0.wireOp",EDGE,"E10.2.3"),sQuery(id+"F0.wireOp",EDGE,"E10.2.4"),sQuery(id+"F0.wireOp",EDGE,"E10.2.5"),sQuery(id+"F0.wireOp",EDGE,"E10.3.0"),sQuery(id+"F0.wireOp",EDGE,"E10.3.1"),sQuery(id+"F0.wireOp",EDGE,"E10.3.2"),sQuery(id+"F0.wireOp",EDGE,"E10.3.3"),sQuery(id+"F0.wireOp",EDGE,"E10.3.4"),sQuery(id+"F0.wireOp",EDGE,"E10.3.5"),sQuery(id+"F0.wireOp",EDGE,"E10.4.0"),sQuery(id+"F0.wireOp",EDGE,"E10.4.1"),sQuery(id+"F0.wireOp",EDGE,"E10.4.2"),sQuery(id+"F0.wireOp",EDGE,"E10.4.3"),sQuery(id+"F0.wireOp",EDGE,"E10.4.4"),sQuery(id+"F0.wireOp",EDGE,"E10.4.5"),sQuery(id+"F0.wireOp",EDGE,"E10.5.0"),sQuery(id+"F0.wireOp",EDGE,"E10.5.1"),sQuery(id+"F0.wireOp",EDGE,"E10.5.2"),sQuery(id+"F0.wireOp",EDGE,"E10.5.3"),sQuery(id+"F0.wireOp",EDGE,"E10.5.4"),sQuery(id+"F0.wireOp",EDGE,"E10.5.5")])],"isStart":false});
            var sketch = newSketch(context, id + "F3", { "sketchPlane" : qUnion([Q0])});
            skLineSegment(sketch, "E17", {"start": v(-14.33, 27.34) * mm, "end": v(-16.5, 26.08) * mm});
            skLineSegment(sketch, "E18", {"start": v(-7.17, 14.92) * mm, "end": v(-9.34, 13.67) * mm});
            skLineSegment(sketch, "E19", {"start": v(16.5, 1.25) * mm, "end": v(16.5, -1.25) * mm});
            skLineSegment(sketch, "E20", {"start": v(30.84, 1.25) * mm, "end": v(30.84, -1.25) * mm});
            skLineSegment(sketch, "E21", {"start": v(-7.17, -14.92) * mm, "end": v(-9.34, -13.67) * mm});
            skLineSegment(sketch, "E22", {"start": v(-16.5, -26.08) * mm, "end": v(-14.33, -27.34) * mm});
            skSolve(sketch);
        }
        {
            var Q0;
            Q0 = qSketchRegion(id + "F3", true);
            var Q1;
            Q1=makeQuery(id+"F3.imprint","IMPRINT",FACE,{"disambiguationData":[TD([[makeQuery(id+"F3.imprint","IMPRINT",EDGE,{"derivedFrom":sQuery(id+"F3.wireOp",EDGE,"E17")}),1.0]])]});
            var Q2;
            Q2=makeQuery(id+"F3.imprint","IMPRINT",FACE,{"disambiguationData":[TD([[makeQuery(id+"F3.imprint","IMPRINT",EDGE,{"derivedFrom":sQuery(id+"F3.wireOp",EDGE,"E21")}),1.0]])]});
            var Q3;
            Q3=makeQuery(id+"F3.imprint","IMPRINT",FACE,{"disambiguationData":[TD([[makeQuery(id+"F3.imprint","IMPRINT",EDGE,{"derivedFrom":sQuery(id+"F3.wireOp",EDGE,"E19")}),1.0]])]});
            extrude(context, id + "F4", {"entities" : qUnion([Q0, Q1, Q2, Q3]), "operationType" : NewBodyOperationType.REMOVE, "oppositeDirection" : true, "depth" : 25.4 * mm});
        }
    });
